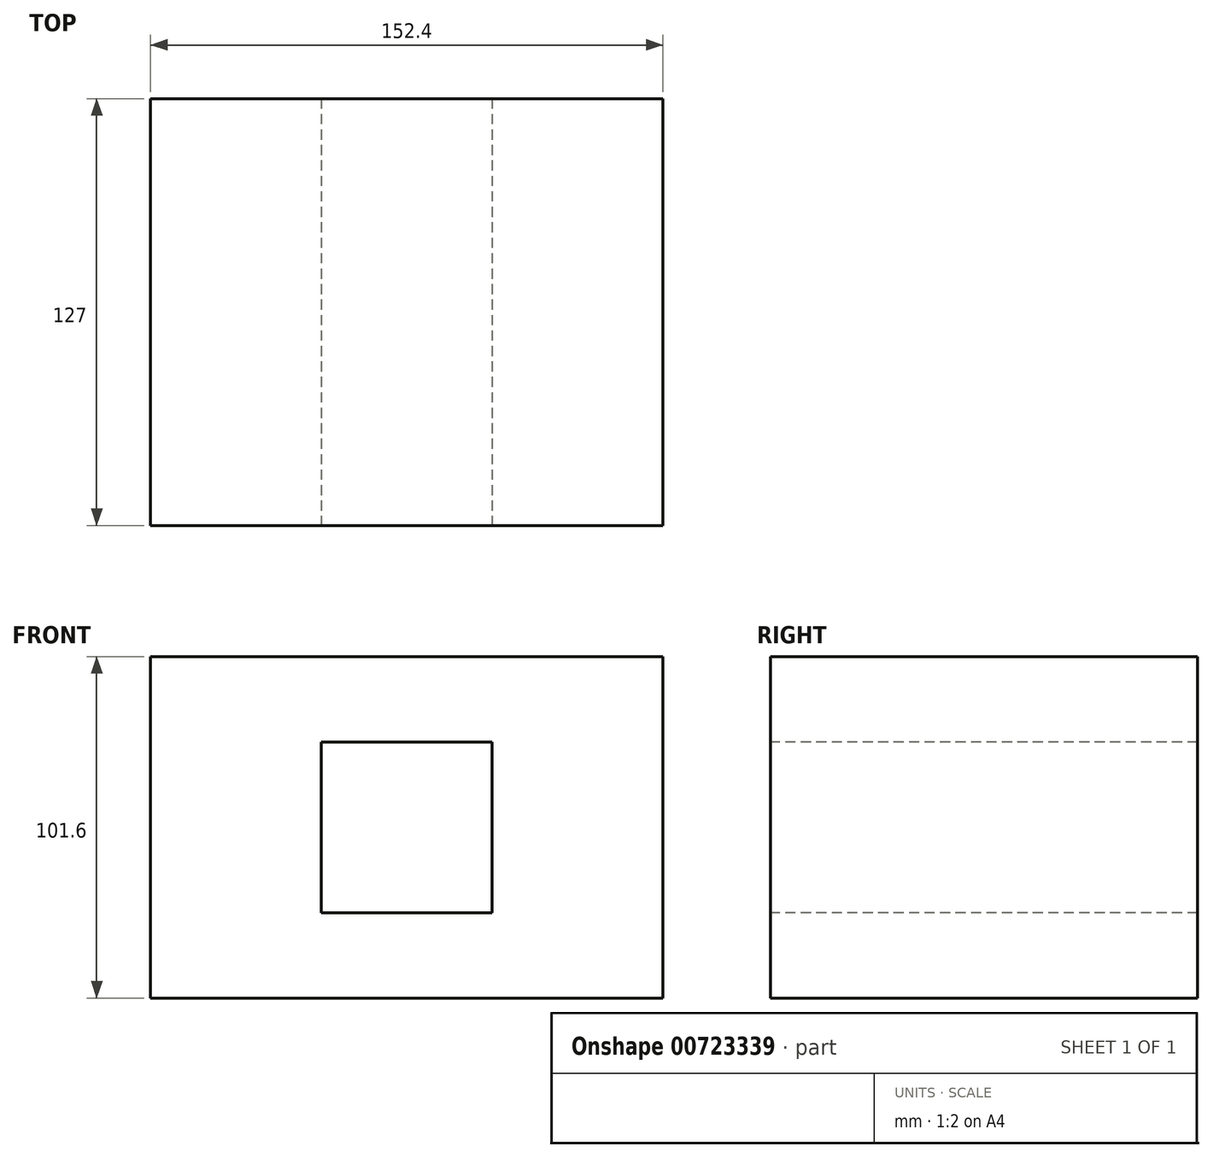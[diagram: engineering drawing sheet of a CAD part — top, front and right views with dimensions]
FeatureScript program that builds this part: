
annotation { "Feature Type Name" : "Feature", "Feature Type Description" : "" }
export const myFeature = defineFeature(function(context is Context, id is Id, definition is map)
    precondition{}
    {
        {
            var Q0;
            Q0=qCreatedBy(makeId("Front.planeOp"),FACE);
            var sketch = newSketch(context, id + "F0", { "sketchPlane" : qUnion([Q0])});
            skLineSegment(sketch, "E0", {"start": v(-67.6, -52.12) * mm, "end": v(84.8, -52.12) * mm});
            skLineSegment(sketch, "E1", {"start": v(84.8, -52.12) * mm, "end": v(84.8, 49.48) * mm});
            skLineSegment(sketch, "E2", {"start": v(84.8, 49.48) * mm, "end": v(-67.6, 49.48) * mm});
            skLineSegment(sketch, "E3", {"start": v(-67.6, 49.48) * mm, "end": v(-67.6, -52.12) * mm});
            skSolve(sketch);
        }
        {
            var Q0;
            Q0=makeQuery(id+"F0.imprint","IMPRINT",FACE,{"disambiguationData":[TD([[makeQuery(id+"F0.imprint","IMPRINT",EDGE,{"derivedFrom":sQuery(id+"F0.wireOp",EDGE,"E0")}),1.0]])]});
            extrude(context, id + "F1", {"entities" : qUnion([Q0]), "depth" : 127 * mm, "offsetDistance" : 25.4 * mm});
        }
        {
            var Q0;
            Q0=makeQuery(id+"F1.opExtrude","CAP_FACE",FACE,{"disambiguationData":[OSD([sQuery(id+"F0.wireOp",EDGE,"E0"),sQuery(id+"F0.wireOp",EDGE,"E1"),sQuery(id+"F0.wireOp",EDGE,"E2"),sQuery(id+"F0.wireOp",EDGE,"E3")])],"isStart":false});
            var sketch = newSketch(context, id + "F2", { "sketchPlane" : qUnion([Q0])});
            skLineSegment(sketch, "E4", {"start": v(3.26, 49.48) * mm, "end": v(3.26, 24.08) * mm});
            skLineSegment(sketch, "E5", {"start": v(6.18, -52.12) * mm, "end": v(6.18, -26.72) * mm});
            skLineSegment(sketch, "E6", {"start": v(84.8, -1.32) * mm, "end": v(34, -1.32) * mm});
            skLineSegment(sketch, "E7", {"start": v(-67.6, -1.32) * mm, "end": v(-16.8, -1.32) * mm});
            skLineSegment(sketch, "E8", {"start": v(-16.8, 24.08) * mm, "end": v(3.26, 24.08) * mm});
            skLineSegment(sketch, "E9", {"start": v(-16.8, 24.08) * mm, "end": v(-16.8, -26.72) * mm});
            skLineSegment(sketch, "E10", {"start": v(-16.8, -26.72) * mm, "end": v(34, -26.72) * mm});
            skLineSegment(sketch, "E11", {"start": v(34, -26.72) * mm, "end": v(34, 24.08) * mm});
            skLineSegment(sketch, "E12", {"start": v(34, 24.08) * mm, "end": v(3.26, 24.08) * mm});
            skSolve(sketch);
        }
        {
            var Q0;
            {var subQ5=sQuery(id+"F2.wireOp",EDGE,"E8");Q0=makeQuery(id+"F2.imprint","IMPRINT",FACE,{"disambiguationData":[TD([[makeQuery(id+"F2.imprint","IMPRINT",EDGE,{"derivedFrom":subQ5}),-1.0]])]});}
            extrude(context, id + "F3", {"entities" : qUnion([Q0]), "operationType" : NewBodyOperationType.REMOVE, "oppositeDirection" : true, "depth" : 127 * mm, "offsetDistance" : 25.4 * mm});
        }
    });
